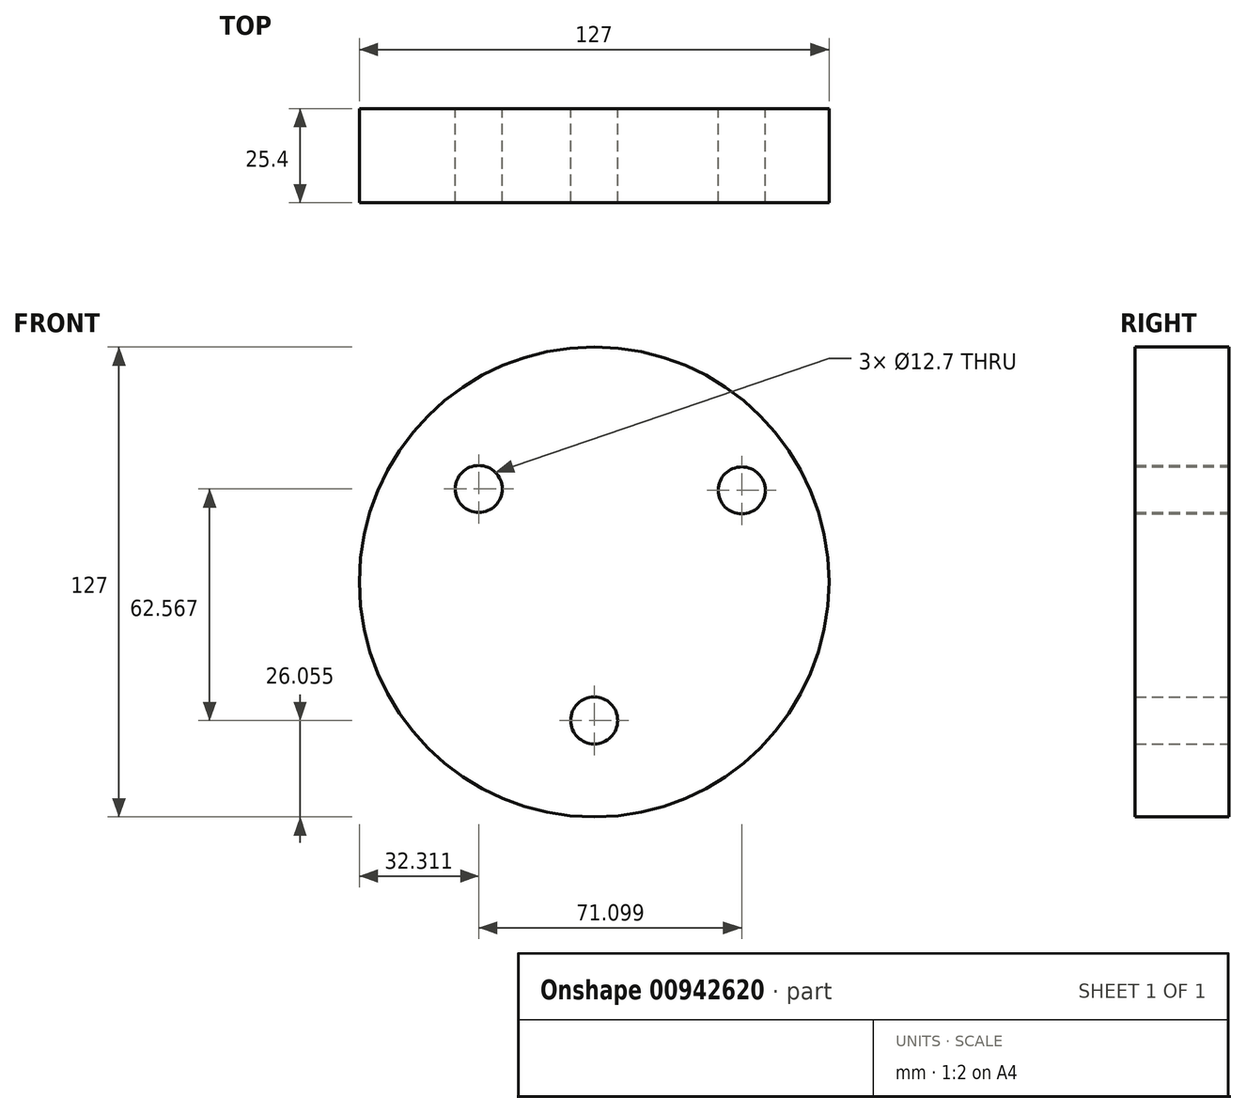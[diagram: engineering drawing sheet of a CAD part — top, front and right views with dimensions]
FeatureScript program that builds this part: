
annotation { "Feature Type Name" : "Feature", "Feature Type Description" : "" }
export const myFeature = defineFeature(function(context is Context, id is Id, definition is map)
    precondition{}
    {
        {
            var Q0;
            Q0=qCreatedBy(makeId("Front.planeOp"),FACE);
            var sketch = newSketch(context, id + "F0", { "sketchPlane" : qUnion([Q0])});
            skCircle(sketch, "E0", {"center": v(0, 0) * mm, "radius": 63.5 * mm});
            skCircle(sketch, "E1", {"center": v(-31.19, 25.12) * mm, "radius": 6.35 * mm});
            skCircle(sketch, "E2", {"center": v(0, -37.45) * mm, "radius": 6.35 * mm});
            skCircle(sketch, "E3", {"center": v(39.91, 24.74) * mm, "radius": 6.35 * mm});
            skSolve(sketch);
        }
        {
            var Q0;
            Q0=makeQuery(id+"F0.imprint","IMPRINT",FACE,{"disambiguationData":[TD([[makeQuery(id+"F0.imprint","IMPRINT",EDGE,{"derivedFrom":sQuery(id+"F0.wireOp",EDGE,"E0")}),1.0]])]});
            extrude(context, id + "F1", {"entities" : qUnion([Q0]), "depth" : 25.4 * mm, "offsetDistance" : 25.4 * mm});
        }
    });
